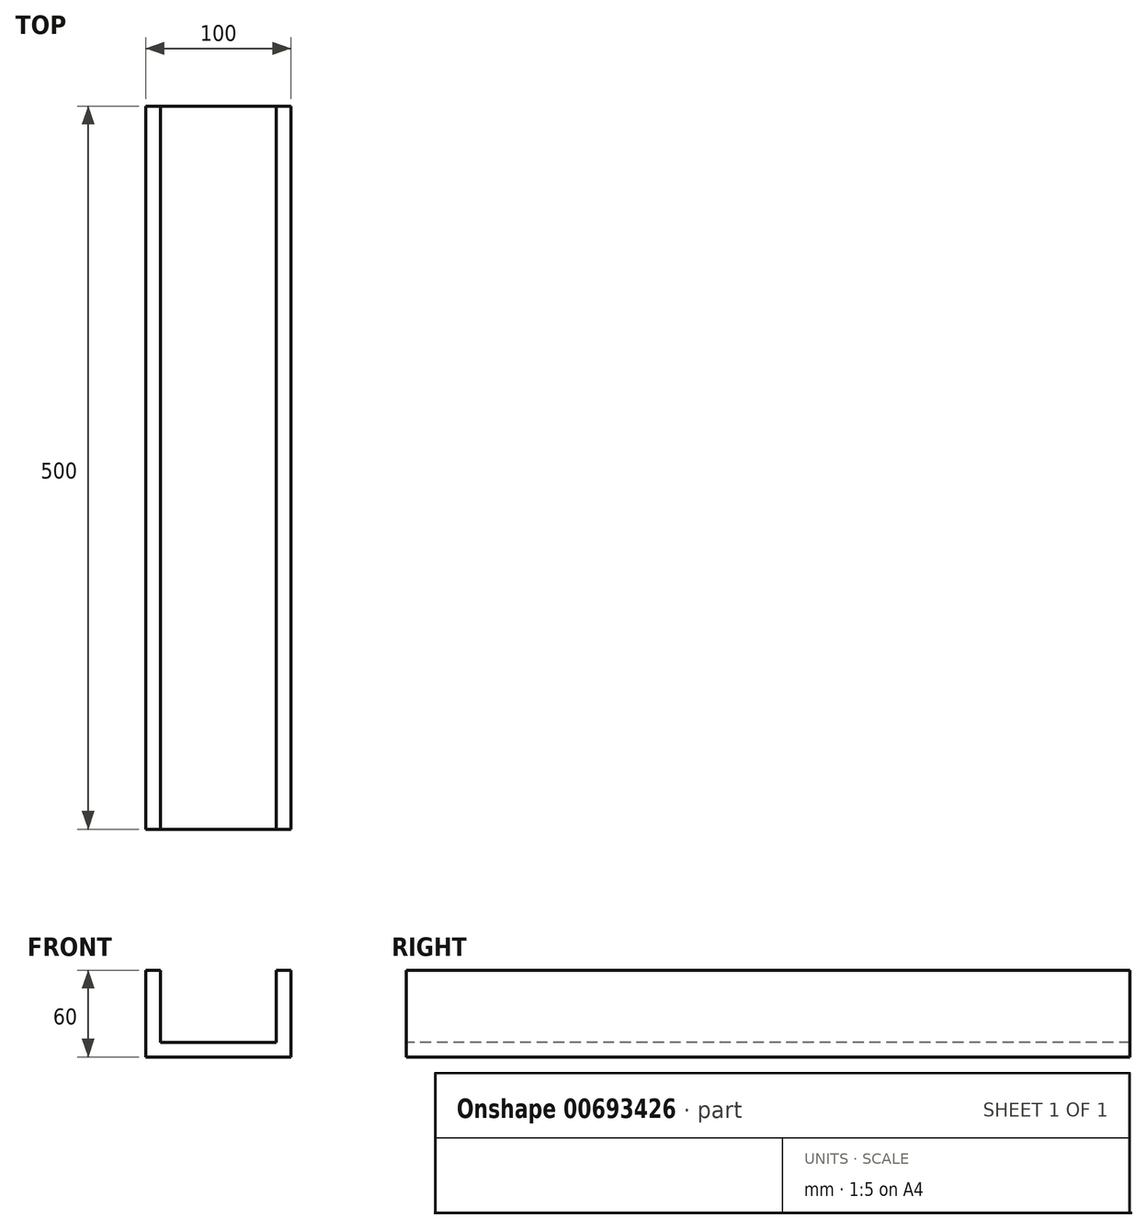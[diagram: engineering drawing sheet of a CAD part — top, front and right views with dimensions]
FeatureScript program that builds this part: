
annotation { "Feature Type Name" : "Feature", "Feature Type Description" : "" }
export const myFeature = defineFeature(function(context is Context, id is Id, definition is map)
    precondition{}
    {
        {
            var Q0;
            Q0=qCreatedBy(makeId("Front.planeOp"),FACE);
            var sketch = newSketch(context, id + "F0", { "sketchPlane" : qUnion([Q0])});
            skLineSegment(sketch, "E0", {"start": v(-50, 0) * mm, "end": v(50, 0) * mm});
            skLineSegment(sketch, "E1", {"start": v(50, 0) * mm, "end": v(50, 60) * mm});
            skLineSegment(sketch, "E2", {"start": v(50, 60) * mm, "end": v(40, 60) * mm});
            skLineSegment(sketch, "E3", {"start": v(40, 60) * mm, "end": v(40, 10) * mm});
            skLineSegment(sketch, "E4", {"start": v(40, 10) * mm, "end": v(-40, 10) * mm});
            skLineSegment(sketch, "E5", {"start": v(-40, 10) * mm, "end": v(-40, 60) * mm});
            skLineSegment(sketch, "E6", {"start": v(-40, 60) * mm, "end": v(-50, 60) * mm});
            skLineSegment(sketch, "E7", {"start": v(-50, 60) * mm, "end": v(-50, 0) * mm});
            skLineSegment(sketch, "E8", {"start": v(0, 0) * mm, "end": v(0, 10) * mm, "construction": true});
            skSolve(sketch);
        }
        {
            var Q0;
            Q0 = qSketchRegion(id + "F0", true);
            extrude(context, id + "F1", {"entities" : qUnion([Q0]), "oppositeDirection" : true, "depth" : 500 * mm, "offsetDistance" : 25.4 * mm});
        }
    });
